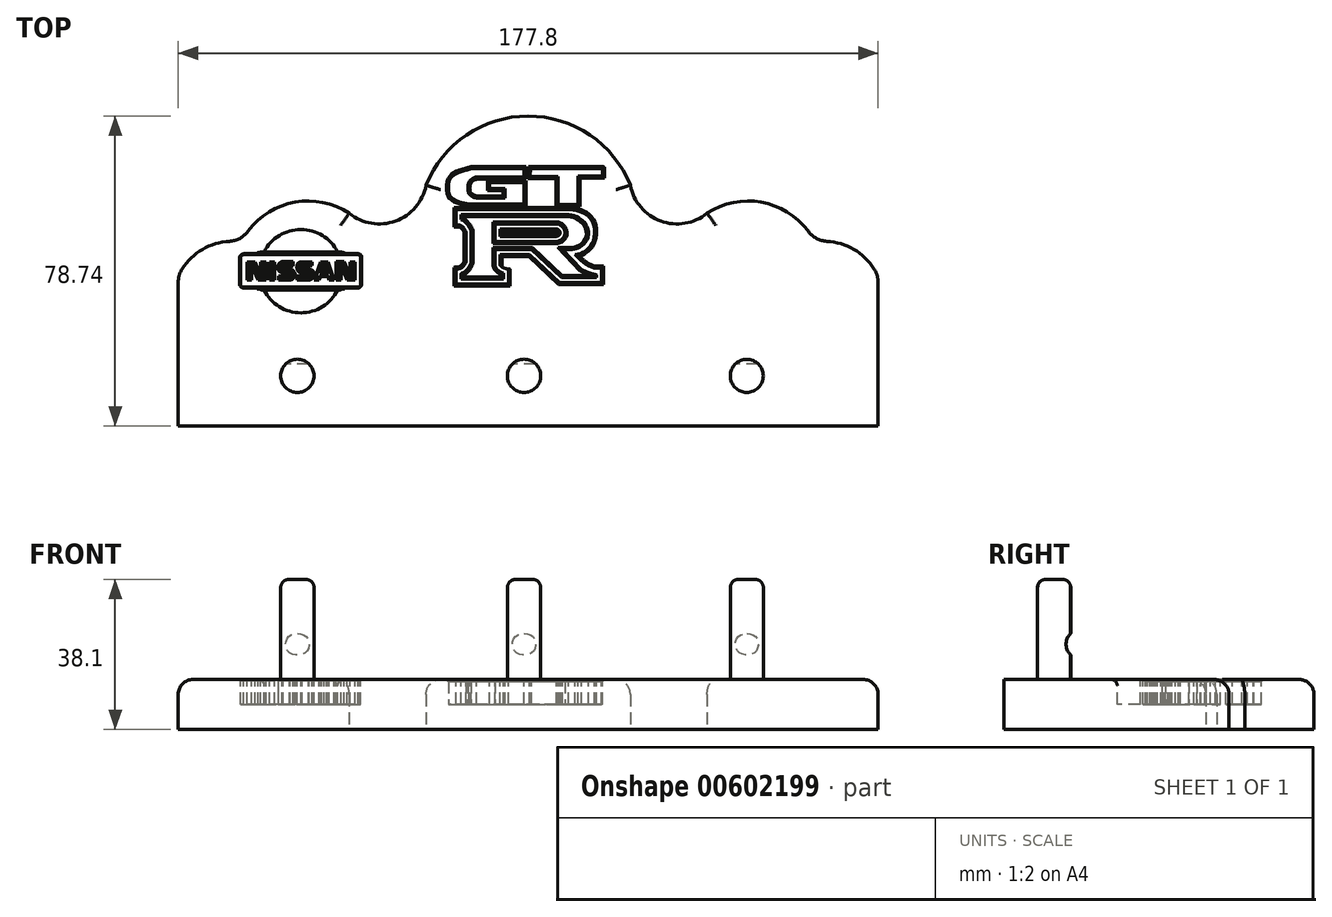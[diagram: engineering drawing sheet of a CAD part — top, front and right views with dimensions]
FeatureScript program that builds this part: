
annotation { "Feature Type Name" : "Feature", "Feature Type Description" : "" }
export const myFeature = defineFeature(function(context is Context, id is Id, definition is map)
    precondition{}
    {
        {
            var Q0;
            Q0=qCreatedBy(makeId("Top.planeOp"),FACE);
            var sketch = newSketch(context, id + "F0", { "sketchPlane" : qUnion([Q0])});
            skLineSegment(sketch, "E0", {"start": v(0, 0) * mm, "end": v(88.9, 0) * mm});
            skLineSegment(sketch, "E1", {"start": v(0, 0) * mm, "end": v(0, 36.5) * mm});
            skArc(sketch, "E2", {"start": v(44.68, 53.17) * mm, "mid": v(30.43, 56.97) * mm, "end": v(17.74, 49.47) * mm});
            skArc(sketch, "E3", {"start": v(88.9, 78.74) * mm, "mid": v(71.93, 73) * mm, "end": v(61.94, 58.13) * mm});
            skLineSegment(sketch, "E4", {"start": v(88.9, 95.72) * mm, "end": v(88.9, -40.01) * mm, "construction": true});
            skPoint(sketch, "E4.endSnap0", {"position": v(88.9, 0) * mm});
            skArc(sketch, "E5", {"start": v(43.45, 54.04) * mm, "mid": v(55.21, 52.07) * mm, "end": v(62.95, 61.15) * mm});
            skArc(sketch, "E6", {"start": v(13, 46.92) * mm, "mid": v(6.17, 44.86) * mm, "end": v(1.02, 39.94) * mm});
            skPoint(sketch, "E7.visualSharp", {"position": v(16.07, 46.79) * mm});
            skArc(sketch, "E7.filletArc", {"start": v(13, 46.92) * mm, "mid": v(15.65, 47.67) * mm, "end": v(17.74, 49.47) * mm});
            skArc(sketch, "E8.MirrorCS", {"start": v(88.9, 78.74) * mm, "mid": v(105.87, 73) * mm, "end": v(115.86, 58.13) * mm});
            skArc(sketch, "E9.MirrorCS", {"start": v(134.35, 54.04) * mm, "mid": v(122.59, 52.07) * mm, "end": v(114.85, 61.15) * mm});
            skArc(sketch, "E10.MirrorCS", {"start": v(133.12, 53.17) * mm, "mid": v(147.37, 56.97) * mm, "end": v(160.06, 49.47) * mm});
            skPoint(sketch, "E11.MirrorP", {"position": v(161.73, 46.79) * mm});
            skArc(sketch, "E12.MirrorCS", {"start": v(164.8, 46.92) * mm, "mid": v(171.63, 44.86) * mm, "end": v(176.78, 39.94) * mm});
            skLineSegment(sketch, "E13.MirrorCS", {"start": v(177.8, 0) * mm, "end": v(177.8, 36.5) * mm});
            skLineSegment(sketch, "E14.MirrorCS", {"start": v(177.8, 0) * mm, "end": v(88.9, 0) * mm});
            skArc(sketch, "E15.MirrorCS", {"start": v(164.8, 46.92) * mm, "mid": v(162.15, 47.67) * mm, "end": v(160.06, 49.47) * mm});
            skPoint(sketch, "E16.visualSharp", {"position": v(0, 38.1) * mm});
            skArc(sketch, "E16.filletArc", {"start": v(1.02, 39.94) * mm, "mid": v(0.26, 38.29) * mm, "end": v(0, 36.5) * mm});
            skPoint(sketch, "E17.visualSharp", {"position": v(177.8, 38.1) * mm});
            skArc(sketch, "E17.filletArc", {"start": v(177.8, 36.5) * mm, "mid": v(177.54, 38.29) * mm, "end": v(176.78, 39.94) * mm});
            skSolve(sketch);
        }
        {
            var Q0;
            Q0=makeQuery(id+"F0.imprint","IMPRINT",FACE,{"disambiguationData":[TD([[makeQuery(id+"F0.imprint","IMPRINT",EDGE,{"derivedFrom":sQuery(id+"F0.wireOp",EDGE,"E0")}),1.0]])]});
            extrude(context, id + "F1", {"entities" : qUnion([Q0]), "depth" : 12.7 * mm, "offsetDistance" : 25.4 * mm});
        }
        {
            var Q0;
            Q0=makeQuery(id+"F1.opExtrude","CAP_FACE",FACE,{"disambiguationData":[OSD([sQuery(id+"F0.wireOp",EDGE,"E0"),sQuery(id+"F0.wireOp",EDGE,"E1"),sQuery(id+"F0.wireOp",EDGE,"E2"),sQuery(id+"F0.wireOp",EDGE,"E3"),sQuery(id+"F0.wireOp",EDGE,"E5"),sQuery(id+"F0.wireOp",EDGE,"E6"),sQuery(id+"F0.wireOp",EDGE,"E7.filletArc"),sQuery(id+"F0.wireOp",EDGE,"E8.MirrorCS"),sQuery(id+"F0.wireOp",EDGE,"E9.MirrorCS"),sQuery(id+"F0.wireOp",EDGE,"E10.MirrorCS"),sQuery(id+"F0.wireOp",EDGE,"E12.MirrorCS"),sQuery(id+"F0.wireOp",EDGE,"E13.MirrorCS"),sQuery(id+"F0.wireOp",EDGE,"E14.MirrorCS"),sQuery(id+"F0.wireOp",EDGE,"E15.MirrorCS"),sQuery(id+"F0.wireOp",EDGE,"E16.filletArc"),sQuery(id+"F0.wireOp",EDGE,"E17.filletArc")])],"isStart":false});
            var sketch = newSketch(context, id + "F2", { "sketchPlane" : qUnion([Q0])});
            skLineSegment(sketch, "E18", {"start": v(89.5, 65.35) * mm, "end": v(107.82, 65.35) * mm});
            skLineSegment(sketch, "E19", {"start": v(107.82, 65.35) * mm, "end": v(107.82, 63.49) * mm});
            skLineSegment(sketch, "E20", {"start": v(107.82, 63.49) * mm, "end": v(101.51, 63.49) * mm});
            skLineSegment(sketch, "E21", {"start": v(101.51, 63.49) * mm, "end": v(101.51, 56.31) * mm});
            skLineSegment(sketch, "E22", {"start": v(101.51, 56.31) * mm, "end": v(96.44, 56.31) * mm});
            skLineSegment(sketch, "E23", {"start": v(96.44, 56.31) * mm, "end": v(96.44, 63.37) * mm});
            skLineSegment(sketch, "E24", {"start": v(96.44, 63.37) * mm, "end": v(89.39, 63.37) * mm});
            skLineSegment(sketch, "E25", {"start": v(89.39, 63.37) * mm, "end": v(89.5, 65.35) * mm});
            skLineSegment(sketch, "E26", {"start": v(75.75, 57.97) * mm, "end": v(83.05, 57.97) * mm});
            skLineSegment(sketch, "E27", {"start": v(83.05, 57.97) * mm, "end": v(83.05, 60.38) * mm});
            skLineSegment(sketch, "E28", {"start": v(83.05, 60.38) * mm, "end": v(79.09, 60.38) * mm});
            skLineSegment(sketch, "E29", {"start": v(79.09, 60.38) * mm, "end": v(79.09, 61.87) * mm});
            skLineSegment(sketch, "E30", {"start": v(79.09, 61.87) * mm, "end": v(87.81, 61.87) * mm});
            skLineSegment(sketch, "E31", {"start": v(87.81, 61.87) * mm, "end": v(87.81, 56.36) * mm});
            skLineSegment(sketch, "E32", {"start": v(87.81, 56.36) * mm, "end": v(73.89, 56.36) * mm});
            skLineSegment(sketch, "E33", {"start": v(75.8, 63.3) * mm, "end": v(87.81, 63.3) * mm});
            skLineSegment(sketch, "E34", {"start": v(87.81, 63.3) * mm, "end": v(87.81, 65.35) * mm});
            skLineSegment(sketch, "E35", {"start": v(87.81, 65.35) * mm, "end": v(74.45, 65.35) * mm});
            skFitSpline(sketch, "E36", {"points": [v(73.89, 56.36) * mm, v(71.04, 57.04) * mm, v(68.94, 58.71) * mm, v(68.75, 61.93) * mm, v(69.25, 63.04) * mm, v(70.8, 64.22) * mm, v(74.45, 65.35) * mm], "startDerivative": vector(-16.25, 2.89) * mm, "endDerivative": vector(19.65, 4.7) * mm});
            skLineSegment(sketch, "E37", {"start": v(70.61, 54.94) * mm, "end": v(99.1, 54.94) * mm});
            skLineSegment(sketch, "E38", {"start": v(73.17, 48.97) * mm, "end": v(73.15, 42.1) * mm});
            skLineSegment(sketch, "E39", {"start": v(70.55, 39.84) * mm, "end": v(70.55, 36) * mm});
            skLineSegment(sketch, "E40", {"start": v(70.55, 36) * mm, "end": v(83.85, 36) * mm});
            skLineSegment(sketch, "E41", {"start": v(83.85, 36) * mm, "end": v(83.85, 39.89) * mm});
            skLineSegment(sketch, "E42", {"start": v(81.75, 41) * mm, "end": v(81.75, 43.5) * mm});
            skLineSegment(sketch, "E43", {"start": v(81.75, 43.5) * mm, "end": v(89.3, 43.5) * mm});
            skLineSegment(sketch, "E44", {"start": v(89.3, 43.5) * mm, "end": v(96.84, 36.45) * mm});
            skLineSegment(sketch, "E45", {"start": v(96.84, 36.45) * mm, "end": v(107.58, 36.45) * mm});
            skLineSegment(sketch, "E46", {"start": v(107.58, 36.45) * mm, "end": v(107.58, 40.07) * mm});
            skFitSpline(sketch, "E47", {"points": [v(70.55, 39.84) * mm, v(71.8, 40.09) * mm, v(72.7, 40.9) * mm, v(73.15, 42.1) * mm], "startDerivative": vector(3.96, 0.32) * mm, "endDerivative": vector(0, 4.08) * mm});
            skLineSegment(sketch, "E48", {"start": v(96.05, 50.06) * mm, "end": v(81.8, 50.06) * mm});
            skLineSegment(sketch, "E49", {"start": v(81.8, 50.06) * mm, "end": v(81.8, 48.18) * mm});
            skLineSegment(sketch, "E50", {"start": v(81.8, 48.18) * mm, "end": v(96.05, 48.18) * mm});
            skFitSpline(sketch, "E51", {"points": [v(96.05, 50.06) * mm, v(96.77, 49.67) * mm, v(96.97, 48.95) * mm, v(96.64, 48.4) * mm, v(96.05, 48.18) * mm], "startDerivative": vector(3.1, 0) * mm, "endDerivative": vector(-2.74, 0) * mm});
            skLineSegment(sketch, "E52.0", {"start": v(71.9, 53.67) * mm, "end": v(71.9, 52.45) * mm});
            skFitSpline(sketch, "E52.1", {"points": [v(70.76, 52.83) * mm, v(70.92, 52.79) * mm, v(71.19, 52.72) * mm, v(71.6, 52.58) * mm, v(71.93, 52.44) * mm, v(72.28, 52.26) * mm, v(72.64, 52.02) * mm, v(72.94, 51.76) * mm, v(73.2, 51.5) * mm, v(73.43, 51.23) * mm, v(73.63, 50.98) * mm, v(73.8, 50.73) * mm, v(73.95, 50.51) * mm, v(74.11, 50.24) * mm, v(74.28, 49.9) * mm, v(74.4, 49.46) * mm, v(74.44, 49.13) * mm, v(74.44, 48.97) * mm]});
            skLineSegment(sketch, "E52.2", {"start": v(74.44, 48.97) * mm, "end": v(74.42, 42.1) * mm});
            skFitSpline(sketch, "E52.3", {"points": [v(70.65, 38.57) * mm, v(70.82, 38.59) * mm, v(71.09, 38.6) * mm, v(71.5, 38.67) * mm, v(71.84, 38.75) * mm, v(72.14, 38.85) * mm, v(72.4, 38.96) * mm, v(72.63, 39.09) * mm, v(72.9, 39.27) * mm, v(73.27, 39.58) * mm, v(73.56, 39.93) * mm, v(73.8, 40.26) * mm, v(73.99, 40.55) * mm, v(74.15, 40.87) * mm, v(74.34, 41.36) * mm, v(74.42, 41.8) * mm, v(74.42, 42.1) * mm]});
            skLineSegment(sketch, "E52.4", {"start": v(71.82, 38.75) * mm, "end": v(71.82, 37.28) * mm});
            skLineSegment(sketch, "E52.5", {"start": v(71.9, 53.67) * mm, "end": v(99.1, 53.67) * mm});
            skLineSegment(sketch, "E52.6", {"start": v(71.82, 37.28) * mm, "end": v(82.58, 37.28) * mm});
            skLineSegment(sketch, "E52.7", {"start": v(106.31, 37.72) * mm, "end": v(106.31, 38.4) * mm});
            skFitSpline(sketch, "E52.8", {"points": [v(102.42, 39.81) * mm, v(102.5, 39.76) * mm, v(102.68, 39.67) * mm, v(103.05, 39.49) * mm, v(103.45, 39.3) * mm, v(103.9, 39.1) * mm, v(104.25, 38.96) * mm, v(104.61, 38.83) * mm, v(105.1, 38.68) * mm, v(105.7, 38.53) * mm, v(106.63, 38.33) * mm, v(107.24, 38.25) * mm, v(107.62, 38.2) * mm]});
            skLineSegment(sketch, "E52.11", {"start": v(97.34, 37.72) * mm, "end": v(106.31, 37.72) * mm});
            skLineSegment(sketch, "E52.12", {"start": v(89.8, 44.78) * mm, "end": v(97.34, 37.72) * mm});
            skLineSegment(sketch, "E52.13", {"start": v(80.48, 44.78) * mm, "end": v(89.8, 44.78) * mm});
            skLineSegment(sketch, "E52.14", {"start": v(80.48, 41.03) * mm, "end": v(80.48, 44.78) * mm});
            skFitSpline(sketch, "E52.15", {"points": [v(80.48, 41.03) * mm, v(80.48, 40.94) * mm, v(80.5, 40.75) * mm, v(80.56, 40.48) * mm, v(80.67, 40.24) * mm, v(80.83, 39.99) * mm, v(80.96, 39.84) * mm, v(81.04, 39.76) * mm, v(81.09, 39.7) * mm, v(81.15, 39.65) * mm, v(81.24, 39.57) * mm, v(81.36, 39.46) * mm, v(81.54, 39.32) * mm, v(81.75, 39.18) * mm, v(81.93, 39.08) * mm, v(82.14, 38.99) * mm, v(82.37, 38.9) * mm, v(82.71, 38.8) * mm, v(82.99, 38.75) * mm, v(83.16, 38.71) * mm, v(83.32, 38.67) * mm, v(83.43, 38.65) * mm, v(83.5, 38.63) * mm]});
            skLineSegment(sketch, "E52.16", {"start": v(82.58, 37.28) * mm, "end": v(82.58, 38.84) * mm});
            skFitSpline(sketch, "E53", {"points": [v(99.1, 53.67) * mm, v(100.84, 53.33) * mm, v(102.68, 52.18) * mm, v(103.86, 50.66) * mm, v(104.2, 49.02) * mm, v(103.86, 47.38) * mm, v(102.96, 46.12) * mm, v(101.7, 45.28) * mm, v(99.8, 44.85) * mm, v(97.67, 44.82) * mm], "startDerivative": vector(15.3, -1.57) * mm, "endDerivative": vector(-17.73, 0.43) * mm});
            skLineSegment(sketch, "E54", {"start": v(97.67, 44.82) * mm, "end": v(102.42, 39.81) * mm});
            skLineSegment(sketch, "E55", {"start": v(70.61, 54.94) * mm, "end": v(70.61, 51.01) * mm});
            skFitSpline(sketch, "E56", {"points": [v(70.61, 51.01) * mm, v(71.55, 51.03) * mm, v(72.28, 50.57) * mm, v(72.9, 49.76) * mm, v(73.17, 48.97) * mm], "startDerivative": vector(3.81, -0.71) * mm, "endDerivative": vector(0.74, -3.33) * mm});
            skLineSegment(sketch, "E57.0", {"start": v(96.05, 51.33) * mm, "end": v(80.53, 51.33) * mm});
            skFitSpline(sketch, "E57.1", {"points": [v(96.05, 51.33) * mm, v(96.23, 51.33) * mm, v(96.58, 51.28) * mm, v(97.03, 51.1) * mm, v(97.4, 50.85) * mm, v(97.7, 50.55) * mm, v(97.95, 50.2) * mm, v(98.13, 49.82) * mm, v(98.24, 49.4) * mm, v(98.27, 48.96) * mm, v(98.2, 48.5) * mm, v(98.02, 48.09) * mm, v(97.8, 47.74) * mm, v(97.51, 47.45) * mm, v(97.19, 47.21) * mm, v(96.71, 46.99) * mm, v(96.32, 46.91) * mm, v(96.05, 46.91) * mm]});
            skLineSegment(sketch, "E57.2", {"start": v(80.53, 46.91) * mm, "end": v(96.05, 46.91) * mm});
            skLineSegment(sketch, "E57.3", {"start": v(80.53, 51.33) * mm, "end": v(80.53, 46.91) * mm});
            skFitSpline(sketch, "E58", {"points": [v(100.8, 43.57) * mm, v(102.39, 43.9) * mm, v(104.04, 44.93) * mm, v(105.07, 46.22) * mm, v(105.7, 48.24) * mm, v(105.66, 50.67) * mm, v(104.85, 52.51) * mm, v(103.57, 53.84) * mm, v(101.98, 54.5) * mm, v(100.33, 54.94) * mm, v(99.1, 54.94) * mm], "startDerivative": vector(16.67, 2.03) * mm, "endDerivative": vector(-14.4, -1.08) * mm});
            skFitSpline(sketch, "E59", {"points": [v(100.8, 43.57) * mm, v(102.06, 42.4) * mm, v(103.3, 41.25) * mm, v(104.9, 40.4) * mm, v(106.07, 40.11) * mm, v(107.58, 40.07) * mm], "startDerivative": vector(6.1, -5.61) * mm, "endDerivative": vector(8.1, 0.07) * mm});
            skFitSpline(sketch, "E60", {"points": [v(75.8, 63.3) * mm, v(74.95, 62.93) * mm, v(73.99, 62.14) * mm, v(73.62, 61.05) * mm, v(73.6, 59.91) * mm, v(73.92, 58.93) * mm, v(74.56, 58.45) * mm, v(75.1, 58.08) * mm, v(75.75, 57.97) * mm], "startDerivative": vector(-6.7, -2.41) * mm, "endDerivative": vector(6.48, -0.32) * mm});
            skFitSpline(sketch, "E61", {"points": [v(81.75, 41) * mm, v(81.84, 40.74) * mm, v(82.47, 40.29) * mm, v(83.3, 39.96) * mm, v(83.85, 39.89) * mm], "startDerivative": vector(0.2, -1.53) * mm, "endDerivative": vector(2.22, -0.16) * mm});
            skSolve(sketch);
        }
        {
            var Q0;
            Q0=makeQuery(id+"F2.imprint","IMPRINT",FACE,{"disambiguationData":[TD([[makeQuery(id+"F2.imprint","IMPRINT",EDGE,{"derivedFrom":sQuery(id+"F2.wireOp",EDGE,"E26")}),-1.0]])]});
            var Q1;
            Q1=makeQuery(id+"F2.imprint","IMPRINT",FACE,{"disambiguationData":[TD([[makeQuery(id+"F2.imprint","IMPRINT",EDGE,{"derivedFrom":sQuery(id+"F2.wireOp",EDGE,"E18")}),-1.0]])]});
            var Q2;
            Q2=makeQuery(id+"F2.imprint","IMPRINT",FACE,{"disambiguationData":[TD([[makeQuery(id+"F2.imprint","IMPRINT",EDGE,{"derivedFrom":sQuery(id+"F2.wireOp",EDGE,"E37")}),-1.0]])]});
            var Q3;
            Q3=makeQuery(id+"F2.imprint","IMPRINT",FACE,{"disambiguationData":[TD([[makeQuery(id+"F2.imprint","IMPRINT",EDGE,{"derivedFrom":sQuery(id+"F2.wireOp",EDGE,"E48")}),-1.0]])]});
            extrude(context, id + "F3", {"entities" : qUnion([Q0, Q1, Q2, Q3]), "operationType" : NewBodyOperationType.REMOVE, "oppositeDirection" : true, "depth" : 6.35 * mm, "offsetDistance" : 25.4 * mm});
        }
        {
            var Q0;
            Q0=makeQuery(id+"F3.boolean.opBoolean","COPY",EDGE,{"derivedFrom":makeQuery(id+"F3.opExtrude","CAP_EDGE",EDGE,{"disambiguationData":[OSD([sQuery(id+"F2.wireOp",EDGE,"E18")])],"isStart":true})});
            var Q1;
            Q1=makeQuery(id+"F3.boolean.opBoolean","COPY",EDGE,{"derivedFrom":makeQuery(id+"F3.opExtrude","CAP_EDGE",EDGE,{"disambiguationData":[OSD([sQuery(id+"F2.wireOp",EDGE,"E25")])],"isStart":true})});
            var Q2;
            Q2=makeQuery(id+"F3.boolean.opBoolean","COPY",EDGE,{"derivedFrom":makeQuery(id+"F3.opExtrude","CAP_EDGE",EDGE,{"disambiguationData":[OSD([sQuery(id+"F2.wireOp",EDGE,"E24")])],"isStart":true})});
            var Q3;
            Q3=makeQuery(id+"F3.boolean.opBoolean","COPY",EDGE,{"derivedFrom":makeQuery(id+"F3.opExtrude","CAP_EDGE",EDGE,{"disambiguationData":[OSD([sQuery(id+"F2.wireOp",EDGE,"E23")])],"isStart":true})});
            var Q4;
            Q4=makeQuery(id+"F3.boolean.opBoolean","COPY",EDGE,{"derivedFrom":makeQuery(id+"F3.opExtrude","CAP_EDGE",EDGE,{"disambiguationData":[OSD([sQuery(id+"F2.wireOp",EDGE,"E22")])],"isStart":true})});
            var Q5;
            Q5=makeQuery(id+"F3.boolean.opBoolean","COPY",EDGE,{"derivedFrom":makeQuery(id+"F3.opExtrude","CAP_EDGE",EDGE,{"disambiguationData":[OSD([sQuery(id+"F2.wireOp",EDGE,"E21")])],"isStart":true})});
            var Q6;
            Q6=makeQuery(id+"F3.boolean.opBoolean","COPY",EDGE,{"derivedFrom":makeQuery(id+"F3.opExtrude","CAP_EDGE",EDGE,{"disambiguationData":[OSD([sQuery(id+"F2.wireOp",EDGE,"E20")])],"isStart":true})});
            var Q7;
            Q7=makeQuery(id+"F3.boolean.opBoolean","COPY",EDGE,{"derivedFrom":makeQuery(id+"F3.opExtrude","CAP_EDGE",EDGE,{"disambiguationData":[OSD([sQuery(id+"F2.wireOp",EDGE,"E19")])],"isStart":true})});
            var Q8;
            Q8=makeQuery(id+"F3.boolean.opBoolean","COPY",EDGE,{"derivedFrom":makeQuery(id+"F3.opExtrude","CAP_EDGE",EDGE,{"disambiguationData":[OSD([sQuery(id+"F2.wireOp",EDGE,"E33")])],"isStart":true})});
            var Q9;
            Q9=makeQuery(id+"F3.boolean.opBoolean","COPY",EDGE,{"derivedFrom":makeQuery(id+"F3.opExtrude","CAP_EDGE",EDGE,{"disambiguationData":[OSD([sQuery(id+"F2.wireOp",EDGE,"E35")])],"isStart":true})});
            var Q10;
            Q10=makeQuery(id+"F3.boolean.opBoolean","COPY",EDGE,{"derivedFrom":makeQuery(id+"F3.opExtrude","CAP_EDGE",EDGE,{"disambiguationData":[OSD([sQuery(id+"F2.wireOp",EDGE,"E34")])],"isStart":true})});
            var Q11;
            Q11=makeQuery(id+"F3.boolean.opBoolean","COPY",EDGE,{"derivedFrom":makeQuery(id+"F3.opExtrude","CAP_EDGE",EDGE,{"disambiguationData":[OSD([sQuery(id+"F2.wireOp",EDGE,"E36")])],"isStart":true})});
            var Q12;
            Q12=makeQuery(id+"F3.boolean.opBoolean","COPY",EDGE,{"derivedFrom":makeQuery(id+"F3.opExtrude","CAP_EDGE",EDGE,{"disambiguationData":[OSD([sQuery(id+"F2.wireOp",EDGE,"E60")])],"isStart":true})});
            var Q13;
            Q13=makeQuery(id+"F3.boolean.opBoolean","COPY",EDGE,{"derivedFrom":makeQuery(id+"F3.opExtrude","CAP_EDGE",EDGE,{"disambiguationData":[OSD([sQuery(id+"F2.wireOp",EDGE,"E29")])],"isStart":true})});
            var Q14;
            Q14=makeQuery(id+"F3.boolean.opBoolean","COPY",EDGE,{"derivedFrom":makeQuery(id+"F3.opExtrude","CAP_EDGE",EDGE,{"disambiguationData":[OSD([sQuery(id+"F2.wireOp",EDGE,"E30")])],"isStart":true})});
            var Q15;
            Q15=makeQuery(id+"F3.boolean.opBoolean","COPY",EDGE,{"derivedFrom":makeQuery(id+"F3.opExtrude","CAP_EDGE",EDGE,{"disambiguationData":[OSD([sQuery(id+"F2.wireOp",EDGE,"E28")])],"isStart":true})});
            var Q16;
            Q16=makeQuery(id+"F3.boolean.opBoolean","COPY",EDGE,{"derivedFrom":makeQuery(id+"F3.opExtrude","CAP_EDGE",EDGE,{"disambiguationData":[OSD([sQuery(id+"F2.wireOp",EDGE,"E27")])],"isStart":true})});
            var Q17;
            Q17=makeQuery(id+"F3.boolean.opBoolean","COPY",EDGE,{"derivedFrom":makeQuery(id+"F3.opExtrude","CAP_EDGE",EDGE,{"disambiguationData":[OSD([sQuery(id+"F2.wireOp",EDGE,"E31")])],"isStart":true})});
            var Q18;
            Q18=makeQuery(id+"F3.boolean.opBoolean","COPY",EDGE,{"derivedFrom":makeQuery(id+"F3.opExtrude","CAP_EDGE",EDGE,{"disambiguationData":[OSD([sQuery(id+"F2.wireOp",EDGE,"E32")])],"isStart":true})});
            var Q19;
            Q19=makeQuery(id+"F3.boolean.opBoolean","COPY",EDGE,{"derivedFrom":makeQuery(id+"F3.opExtrude","CAP_EDGE",EDGE,{"disambiguationData":[OSD([sQuery(id+"F2.wireOp",EDGE,"E52.5")])],"isStart":true})});
            var Q20;
            Q20=makeQuery(id+"F3.boolean.opBoolean","SPLIT",FACE,{"disambiguationData":[TD([makeQuery(id+"F3.opExtrude","SWEPT_FACE",FACE,{"disambiguationData":[OSD([sQuery(id+"F2.wireOp",EDGE,"E52.0")])]})])],"derivedFrom":makeQuery(id+"F1.opExtrude","CAP_FACE",FACE,{"disambiguationData":[OSD([sQuery(id+"F0.wireOp",EDGE,"E0"),sQuery(id+"F0.wireOp",EDGE,"E1"),sQuery(id+"F0.wireOp",EDGE,"E2"),sQuery(id+"F0.wireOp",EDGE,"E3"),sQuery(id+"F0.wireOp",EDGE,"E5"),sQuery(id+"F0.wireOp",EDGE,"E6"),sQuery(id+"F0.wireOp",EDGE,"E7.filletArc"),sQuery(id+"F0.wireOp",EDGE,"E8.MirrorCS"),sQuery(id+"F0.wireOp",EDGE,"E9.MirrorCS"),sQuery(id+"F0.wireOp",EDGE,"E10.MirrorCS"),sQuery(id+"F0.wireOp",EDGE,"E12.MirrorCS"),sQuery(id+"F0.wireOp",EDGE,"E13.MirrorCS"),sQuery(id+"F0.wireOp",EDGE,"E14.MirrorCS"),sQuery(id+"F0.wireOp",EDGE,"E15.MirrorCS"),sQuery(id+"F0.wireOp",EDGE,"E16.filletArc"),sQuery(id+"F0.wireOp",EDGE,"E17.filletArc")])],"isStart":false})});
            var Q21;
            Q21=makeQuery(id+"F3.boolean.opBoolean","SPLIT",FACE,{"disambiguationData":[TD([makeQuery(id+"F3.opExtrude","SWEPT_FACE",FACE,{"disambiguationData":[OSD([sQuery(id+"F2.wireOp",EDGE,"E48")])]})])],"derivedFrom":makeQuery(id+"F1.opExtrude","CAP_FACE",FACE,{"disambiguationData":[OSD([sQuery(id+"F0.wireOp",EDGE,"E0"),sQuery(id+"F0.wireOp",EDGE,"E1"),sQuery(id+"F0.wireOp",EDGE,"E2"),sQuery(id+"F0.wireOp",EDGE,"E3"),sQuery(id+"F0.wireOp",EDGE,"E5"),sQuery(id+"F0.wireOp",EDGE,"E6"),sQuery(id+"F0.wireOp",EDGE,"E7.filletArc"),sQuery(id+"F0.wireOp",EDGE,"E8.MirrorCS"),sQuery(id+"F0.wireOp",EDGE,"E9.MirrorCS"),sQuery(id+"F0.wireOp",EDGE,"E10.MirrorCS"),sQuery(id+"F0.wireOp",EDGE,"E12.MirrorCS"),sQuery(id+"F0.wireOp",EDGE,"E13.MirrorCS"),sQuery(id+"F0.wireOp",EDGE,"E14.MirrorCS"),sQuery(id+"F0.wireOp",EDGE,"E15.MirrorCS"),sQuery(id+"F0.wireOp",EDGE,"E16.filletArc"),sQuery(id+"F0.wireOp",EDGE,"E17.filletArc")])],"isStart":false})});
            var Q22;
            Q22=makeQuery(id+"F3.boolean.opBoolean","COPY",EDGE,{"derivedFrom":makeQuery(id+"F3.opExtrude","CAP_EDGE",EDGE,{"disambiguationData":[OSD([sQuery(id+"F2.wireOp",EDGE,"E37")])],"isStart":true})});
            var Q23;
            Q23=makeQuery(id+"F3.boolean.opBoolean","COPY",EDGE,{"derivedFrom":makeQuery(id+"F3.opExtrude","CAP_EDGE",EDGE,{"disambiguationData":[OSD([sQuery(id+"F2.wireOp",EDGE,"E58")])],"isStart":true})});
            var Q24;
            Q24=makeQuery(id+"F3.boolean.opBoolean","COPY",EDGE,{"derivedFrom":makeQuery(id+"F3.opExtrude","CAP_EDGE",EDGE,{"disambiguationData":[OSD([sQuery(id+"F2.wireOp",EDGE,"E41")])],"isStart":true})});
            var Q25;
            Q25=makeQuery(id+"F3.boolean.opBoolean","COPY",EDGE,{"derivedFrom":makeQuery(id+"F3.opExtrude","CAP_EDGE",EDGE,{"disambiguationData":[OSD([sQuery(id+"F2.wireOp",EDGE,"E44")])],"isStart":true})});
            var Q26;
            Q26=makeQuery(id+"F3.boolean.opBoolean","COPY",EDGE,{"derivedFrom":makeQuery(id+"F3.opExtrude","CAP_EDGE",EDGE,{"disambiguationData":[OSD([sQuery(id+"F2.wireOp",EDGE,"E43")])],"isStart":true})});
            var Q27;
            Q27=makeQuery(id+"F3.boolean.opBoolean","COPY",EDGE,{"derivedFrom":makeQuery(id+"F3.opExtrude","CAP_EDGE",EDGE,{"disambiguationData":[OSD([sQuery(id+"F2.wireOp",EDGE,"E59")])],"isStart":true})});
            var Q28;
            Q28=makeQuery(id+"F3.boolean.opBoolean","COPY",EDGE,{"derivedFrom":makeQuery(id+"F3.opExtrude","CAP_EDGE",EDGE,{"disambiguationData":[OSD([sQuery(id+"F2.wireOp",EDGE,"E46")])],"isStart":true})});
            var Q29;
            Q29=makeQuery(id+"F3.boolean.opBoolean","COPY",EDGE,{"derivedFrom":makeQuery(id+"F3.opExtrude","CAP_EDGE",EDGE,{"disambiguationData":[OSD([sQuery(id+"F2.wireOp",EDGE,"E45")])],"isStart":true})});
            var Q30;
            Q30=makeQuery(id+"F3.boolean.opBoolean","COPY",EDGE,{"derivedFrom":makeQuery(id+"F3.opExtrude","CAP_EDGE",EDGE,{"disambiguationData":[OSD([sQuery(id+"F2.wireOp",EDGE,"E40")])],"isStart":true})});
            var Q31;
            Q31=makeQuery(id+"F3.boolean.opBoolean","COPY",EDGE,{"derivedFrom":makeQuery(id+"F3.opExtrude","CAP_EDGE",EDGE,{"disambiguationData":[OSD([sQuery(id+"F2.wireOp",EDGE,"E39")])],"isStart":true})});
            var Q32;
            Q32=makeQuery(id+"F3.boolean.opBoolean","COPY",EDGE,{"derivedFrom":makeQuery(id+"F3.opExtrude","CAP_EDGE",EDGE,{"disambiguationData":[OSD([sQuery(id+"F2.wireOp",EDGE,"E47")])],"isStart":true})});
            var Q33;
            Q33=makeQuery(id+"F3.boolean.opBoolean","COPY",EDGE,{"derivedFrom":makeQuery(id+"F3.opExtrude","CAP_EDGE",EDGE,{"disambiguationData":[OSD([sQuery(id+"F2.wireOp",EDGE,"E38")])],"isStart":true})});
            var Q34;
            Q34=makeQuery(id+"F3.boolean.opBoolean","COPY",EDGE,{"derivedFrom":makeQuery(id+"F3.opExtrude","CAP_EDGE",EDGE,{"disambiguationData":[OSD([sQuery(id+"F2.wireOp",EDGE,"E56")])],"isStart":true})});
            var Q35;
            Q35=makeQuery(id+"F3.boolean.opBoolean","COPY",EDGE,{"derivedFrom":makeQuery(id+"F3.opExtrude","CAP_EDGE",EDGE,{"disambiguationData":[OSD([sQuery(id+"F2.wireOp",EDGE,"E55")])],"isStart":true})});
            chamfer(context, id + "F4", {"entities" : qUnion([Q0, Q1, Q2, Q3, Q4, Q5, Q6, Q7, Q8, Q9, Q10, Q11, Q12, Q13, Q14, Q15, Q16, Q17, Q18, Q19, Q20, Q21, Q22, Q23, Q24, Q25, Q26, Q27, Q28, Q29, Q30, Q31, Q32, Q33, Q34, Q35]), "width" : 0.5 * mm, "tangentPropagation" : true});
        }
        {
            var Q0;
            {var subQ0=sQuery(id+"F0.wireOp",EDGE,"E12.MirrorCS");var subQ1=sQuery(id+"F0.wireOp",EDGE,"E10.MirrorCS");var subQ2=sQuery(id+"F0.wireOp",EDGE,"E9.MirrorCS");var subQ3=sQuery(id+"F0.wireOp",EDGE,"E7.filletArc");var subQ4=sQuery(id+"F0.wireOp",EDGE,"E6");var subQ5=sQuery(id+"F0.wireOp",EDGE,"E5");var subQ6=sQuery(id+"F0.wireOp",EDGE,"E14.MirrorCS");var subQ7=sQuery(id+"F0.wireOp",EDGE,"E0");var subQ8=sQuery(id+"F0.wireOp",EDGE,"E1");var subQ9=sQuery(id+"F0.wireOp",EDGE,"E2");var subQ10=sQuery(id+"F0.wireOp",EDGE,"E8.MirrorCS");var subQ11=sQuery(id+"F0.wireOp",EDGE,"E3");var subQ12=sQuery(id+"F0.wireOp",EDGE,"E13.MirrorCS");var subQ13=sQuery(id+"F0.wireOp",EDGE,"E15.MirrorCS");var subQ14=sQuery(id+"F0.wireOp",EDGE,"E16.filletArc");var subQ15=sQuery(id+"F0.wireOp",EDGE,"E17.filletArc");Q0=makeQuery(id+"F3.boolean.opBoolean","SPLIT",FACE,{"disambiguationData":[TD([makeQuery(id+"F1.opExtrude","SWEPT_FACE",FACE,{"disambiguationData":[OSD([subQ8])]})])],"derivedFrom":makeQuery(id+"F1.opExtrude","CAP_FACE",FACE,{"disambiguationData":[OSD([subQ7,subQ8,subQ9,subQ11,subQ5,subQ4,subQ3,subQ10,subQ2,subQ1,subQ0,subQ12,subQ6,subQ13,subQ14,subQ15])],"isStart":false})});}
            var sketch = newSketch(context, id + "F5", { "sketchPlane" : qUnion([Q0])});
            skArc(sketch, "E62", {"start": v(40.5, 44.26) * mm, "mid": v(31.16, 49.94) * mm, "end": v(21.8, 44.26) * mm});
            skLineSegment(sketch, "E63", {"start": v(21.8, 44.26) * mm, "end": v(40.5, 44.26) * mm});
            skLineSegment(sketch, "E64", {"start": v(21.86, 34.6) * mm, "end": v(40.47, 34.6) * mm});
            skArc(sketch, "E65", {"start": v(21.86, 34.6) * mm, "mid": v(31.16, 28.74) * mm, "end": v(40.47, 34.6) * mm});
            skLineSegment(sketch, "E66", {"start": v(17.43, 37.11) * mm, "end": v(17.43, 41.71) * mm});
            skLineSegment(sketch, "E67", {"start": v(17.43, 41.71) * mm, "end": v(19.53, 41.71) * mm});
            skLineSegment(sketch, "E68", {"start": v(19.53, 41.71) * mm, "end": v(20.96, 38.22) * mm});
            skLineSegment(sketch, "E69", {"start": v(20.96, 38.22) * mm, "end": v(20.96, 41.68) * mm});
            skLineSegment(sketch, "E70", {"start": v(20.96, 41.68) * mm, "end": v(22.3, 41.68) * mm});
            skLineSegment(sketch, "E71", {"start": v(22.3, 41.68) * mm, "end": v(22.3, 37.05) * mm});
            skLineSegment(sketch, "E72", {"start": v(22.3, 37.05) * mm, "end": v(20.23, 37.05) * mm});
            skLineSegment(sketch, "E73", {"start": v(20.23, 37.05) * mm, "end": v(18.7, 40.71) * mm});
            skLineSegment(sketch, "E74", {"start": v(18.7, 40.71) * mm, "end": v(18.7, 37.11) * mm});
            skLineSegment(sketch, "E75", {"start": v(18.7, 37.11) * mm, "end": v(17.43, 37.11) * mm});
            skLineSegment(sketch, "E76", {"start": v(23.21, 41.7) * mm, "end": v(24.52, 41.7) * mm});
            skLineSegment(sketch, "E77", {"start": v(24.52, 41.7) * mm, "end": v(24.52, 37.06) * mm});
            skLineSegment(sketch, "E78", {"start": v(24.52, 37.06) * mm, "end": v(23.23, 37.06) * mm});
            skLineSegment(sketch, "E79", {"start": v(23.23, 37.06) * mm, "end": v(23.21, 41.7) * mm});
            skLineSegment(sketch, "E80", {"start": v(34.46, 37.06) * mm, "end": v(36.12, 41.7) * mm});
            skLineSegment(sketch, "E81", {"start": v(36.12, 41.7) * mm, "end": v(38.01, 41.7) * mm});
            skLineSegment(sketch, "E82", {"start": v(38.01, 41.7) * mm, "end": v(39.65, 37.08) * mm});
            skLineSegment(sketch, "E83", {"start": v(39.65, 37.08) * mm, "end": v(38.36, 37.08) * mm});
            skLineSegment(sketch, "E84", {"start": v(38.36, 37.08) * mm, "end": v(38.05, 37.9) * mm});
            skLineSegment(sketch, "E85", {"start": v(38.05, 37.9) * mm, "end": v(36.1, 37.9) * mm});
            skLineSegment(sketch, "E86", {"start": v(36.1, 37.9) * mm, "end": v(35.76, 37.04) * mm});
            skLineSegment(sketch, "E87", {"start": v(35.76, 37.04) * mm, "end": v(34.46, 37.06) * mm});
            skLineSegment(sketch, "E88", {"start": v(36.42, 38.94) * mm, "end": v(37.04, 40.68) * mm});
            skLineSegment(sketch, "E89", {"start": v(37.04, 40.68) * mm, "end": v(37.72, 38.92) * mm});
            skLineSegment(sketch, "E90", {"start": v(37.72, 38.92) * mm, "end": v(36.42, 38.94) * mm});
            skLineSegment(sketch, "E91", {"start": v(40.07, 37.09) * mm, "end": v(40.07, 41.72) * mm});
            skLineSegment(sketch, "E92", {"start": v(40.07, 41.72) * mm, "end": v(42.18, 41.72) * mm});
            skLineSegment(sketch, "E93", {"start": v(42.18, 41.72) * mm, "end": v(43.63, 38.18) * mm});
            skLineSegment(sketch, "E94", {"start": v(43.63, 38.18) * mm, "end": v(43.63, 41.69) * mm});
            skLineSegment(sketch, "E95", {"start": v(43.63, 41.69) * mm, "end": v(44.91, 41.69) * mm});
            skLineSegment(sketch, "E96", {"start": v(44.91, 41.69) * mm, "end": v(44.91, 37.06) * mm});
            skLineSegment(sketch, "E97", {"start": v(44.91, 37.06) * mm, "end": v(42.88, 37.06) * mm});
            skLineSegment(sketch, "E98", {"start": v(42.88, 37.06) * mm, "end": v(41.38, 40.73) * mm});
            skLineSegment(sketch, "E99", {"start": v(41.38, 40.73) * mm, "end": v(41.38, 37.07) * mm});
            skLineSegment(sketch, "E100", {"start": v(41.38, 37.07) * mm, "end": v(40.07, 37.09) * mm});
            skLineSegment(sketch, "E101", {"start": v(28.4, 39.86) * mm, "end": v(26.59, 39.86) * mm});
            skLineSegment(sketch, "E102", {"start": v(26.59, 39.86) * mm, "end": v(26.59, 40.68) * mm});
            skLineSegment(sketch, "E103", {"start": v(26.59, 40.68) * mm, "end": v(29.22, 40.68) * mm});
            skLineSegment(sketch, "E104", {"start": v(29.22, 40.68) * mm, "end": v(29.22, 41.72) * mm});
            skLineSegment(sketch, "E105", {"start": v(29.22, 41.72) * mm, "end": v(26.34, 41.72) * mm});
            skLineSegment(sketch, "E106", {"start": v(26.64, 38.92) * mm, "end": v(28.26, 38.92) * mm});
            skLineSegment(sketch, "E107", {"start": v(28.26, 38.92) * mm, "end": v(28.26, 38.13) * mm});
            skLineSegment(sketch, "E108", {"start": v(28.26, 38.13) * mm, "end": v(25.45, 38.13) * mm});
            skLineSegment(sketch, "E109", {"start": v(25.45, 38.13) * mm, "end": v(25.45, 37.08) * mm});
            skLineSegment(sketch, "E110", {"start": v(25.45, 37.08) * mm, "end": v(28.48, 37.08) * mm});
            skFitSpline(sketch, "E111", {"points": [v(26.34, 41.72) * mm, v(25.76, 41.42) * mm, v(25.4, 40.9) * mm, v(25.33, 40.32) * mm, v(25.46, 39.55) * mm, v(25.76, 39.22) * mm, v(26.34, 38.98) * mm, v(26.64, 38.92) * mm], "startDerivative": vector(-4.03, -1.59) * mm, "endDerivative": vector(2.58, -0.3) * mm});
            skPoint(sketch, "E112.3.internal.snap0", {"position": v(28.26, 38.52) * mm});
            skFitSpline(sketch, "E112", {"points": [v(28.4, 39.86) * mm, v(29.03, 39.64) * mm, v(29.47, 39.17) * mm, v(29.66, 38.52) * mm, v(29.47, 37.77) * mm, v(28.92, 37.22) * mm, v(28.48, 37.08) * mm], "startDerivative": vector(3.99, -0.96) * mm, "endDerivative": vector(-3.1, -0.58) * mm});
            skLineSegment(sketch, "E113", {"start": v(31.4, 38.91) * mm, "end": v(33.15, 38.91) * mm});
            skLineSegment(sketch, "E114", {"start": v(33.15, 38.91) * mm, "end": v(33.15, 38.1) * mm});
            skLineSegment(sketch, "E115", {"start": v(33.15, 38.1) * mm, "end": v(30.25, 38.1) * mm});
            skLineSegment(sketch, "E116", {"start": v(30.25, 38.1) * mm, "end": v(30.25, 37.05) * mm});
            skLineSegment(sketch, "E117", {"start": v(30.25, 37.05) * mm, "end": v(33.29, 37.05) * mm});
            skLineSegment(sketch, "E118", {"start": v(31.2, 41.71) * mm, "end": v(34.04, 41.71) * mm});
            skLineSegment(sketch, "E119", {"start": v(34.04, 41.71) * mm, "end": v(34.04, 40.71) * mm});
            skLineSegment(sketch, "E120", {"start": v(34.04, 40.71) * mm, "end": v(31.43, 40.71) * mm});
            skLineSegment(sketch, "E121", {"start": v(31.43, 40.71) * mm, "end": v(31.43, 39.9) * mm});
            skLineSegment(sketch, "E122", {"start": v(31.43, 39.9) * mm, "end": v(33.12, 39.9) * mm});
            skFitSpline(sketch, "E123", {"points": [v(31.4, 38.91) * mm, v(30.86, 39.06) * mm, v(30.4, 39.43) * mm, v(30.17, 39.91) * mm, v(30.14, 40.64) * mm, v(30.38, 41.2) * mm, v(30.73, 41.53) * mm, v(31.2, 41.71) * mm], "startDerivative": vector(-3.88, 0.72) * mm, "endDerivative": vector(3.64, 1.1) * mm});
            skFitSpline(sketch, "E124", {"points": [v(33.12, 39.9) * mm, v(33.64, 39.77) * mm, v(34.13, 39.48) * mm, v(34.44, 38.91) * mm, v(34.48, 38.39) * mm, v(34.37, 37.96) * mm, v(34.14, 37.57) * mm, v(33.77, 37.23) * mm, v(33.29, 37.05) * mm], "startDerivative": vector(4.16, -0.8) * mm, "endDerivative": vector(-4.06, -1.22) * mm});
            skLineSegment(sketch, "E125.bottom", {"start": v(16.6, 43.5) * mm, "end": v(45.83, 43.5) * mm});
            skLineSegment(sketch, "E125.top", {"start": v(16.57, 35.3) * mm, "end": v(45.7, 35.3) * mm});
            skLineSegment(sketch, "E125.left", {"start": v(15.82, 42.7) * mm, "end": v(15.82, 36.13) * mm});
            skLineSegment(sketch, "E125.right", {"start": v(46.35, 42.9) * mm, "end": v(46.35, 35.94) * mm});
            skArc(sketch, "E126", {"start": v(46.35, 42.9) * mm, "mid": v(46.2, 43.3) * mm, "end": v(45.83, 43.5) * mm});
            skArc(sketch, "E127", {"start": v(16.6, 43.5) * mm, "mid": v(16.06, 43.25) * mm, "end": v(15.82, 42.7) * mm});
            skArc(sketch, "E128", {"start": v(15.82, 36.13) * mm, "mid": v(16.03, 35.57) * mm, "end": v(16.57, 35.3) * mm});
            skArc(sketch, "E129", {"start": v(45.7, 35.3) * mm, "mid": v(46.13, 35.5) * mm, "end": v(46.35, 35.94) * mm});
            skSolve(sketch);
        }
        {
            var Q0;
            Q0 = qSketchRegion(id + "F5", true);
            var Q1;
            Q1=makeQuery(id+"F5.imprint","IMPRINT",FACE,{"disambiguationData":[TD([[makeQuery(id+"F5.imprint","IMPRINT",EDGE,{"derivedFrom":sQuery(id+"F5.wireOp",EDGE,"E88")}),-1.0]])]});
            extrude(context, id + "F6", {"entities" : qUnion([Q0, Q1]), "operationType" : NewBodyOperationType.REMOVE, "oppositeDirection" : true, "depth" : 6.35 * mm, "offsetDistance" : 25.4 * mm});
        }
        {
            var Q0;
            {var subQ21=sQuery(id+"F0.wireOp",EDGE,"E12.MirrorCS");var subQ23=sQuery(id+"F0.wireOp",EDGE,"E10.MirrorCS");var subQ25=sQuery(id+"F0.wireOp",EDGE,"E9.MirrorCS");var subQ27=sQuery(id+"F0.wireOp",EDGE,"E7.filletArc");var subQ29=sQuery(id+"F0.wireOp",EDGE,"E6");var subQ33=sQuery(id+"F0.wireOp",EDGE,"E5");var subQ37=sQuery(id+"F0.wireOp",EDGE,"E14.MirrorCS");var subQ38=sQuery(id+"F0.wireOp",EDGE,"E0");var subQ42=sQuery(id+"F0.wireOp",EDGE,"E1");var subQ43=makeQuery(id+"F1.opExtrude","SWEPT_FACE",FACE,{"disambiguationData":[OSD([subQ42])]});var subQ46=sQuery(id+"F0.wireOp",EDGE,"E2");var subQ49=sQuery(id+"F0.wireOp",EDGE,"E8.MirrorCS");var subQ50=sQuery(id+"F0.wireOp",EDGE,"E3");var subQ54=sQuery(id+"F0.wireOp",EDGE,"E13.MirrorCS");var subQ56=sQuery(id+"F0.wireOp",EDGE,"E15.MirrorCS");var subQ58=sQuery(id+"F0.wireOp",EDGE,"E16.filletArc");var subQ61=sQuery(id+"F0.wireOp",EDGE,"E17.filletArc");Q0=makeQuery(id+"F6.boolean.opBoolean","SPLIT",FACE,{"disambiguationData":[TD([subQ43])],"derivedFrom":makeQuery(id+"F3.boolean.opBoolean","SPLIT",FACE,{"disambiguationData":[TD([subQ43])],"derivedFrom":makeQuery(id+"F1.opExtrude","CAP_FACE",FACE,{"disambiguationData":[OSD([subQ38,subQ42,subQ46,subQ50,subQ33,subQ29,subQ27,subQ49,subQ25,subQ23,subQ21,subQ54,subQ37,subQ56,subQ58,subQ61])],"isStart":false})})});}
            var sketch = newSketch(context, id + "F7", { "sketchPlane" : qUnion([Q0])});
            skSolve(sketch);
        }
        {
            var Q0;
            Q0=makeQuery(id+"F1.opExtrude","CAP_EDGE",EDGE,{"disambiguationData":[OSD([sQuery(id+"F0.wireOp",EDGE,"E5")])],"isStart":false});
            var Q1;
            Q1=makeQuery(id+"F1.opExtrude","CAP_EDGE",EDGE,{"disambiguationData":[OSD([sQuery(id+"F0.wireOp",EDGE,"E2")])],"isStart":false});
            var Q2;
            Q2=makeQuery(id+"F1.opExtrude","CAP_EDGE",EDGE,{"disambiguationData":[OSD([sQuery(id+"F0.wireOp",EDGE,"E3"),sQuery(id+"F0.wireOp",EDGE,"E8.MirrorCS")])],"isStart":false});
            var Q3;
            Q3=makeQuery(id+"F1.opExtrude","CAP_EDGE",EDGE,{"disambiguationData":[OSD([sQuery(id+"F0.wireOp",EDGE,"E10.MirrorCS")])],"isStart":false});
            var Q4;
            Q4=makeQuery(id+"F1.opExtrude","CAP_EDGE",EDGE,{"disambiguationData":[OSD([sQuery(id+"F0.wireOp",EDGE,"E9.MirrorCS")])],"isStart":false});
            var Q5;
            Q5=makeQuery(id+"F1.opExtrude","CAP_EDGE",EDGE,{"disambiguationData":[OSD([sQuery(id+"F0.wireOp",EDGE,"E12.MirrorCS")])],"isStart":false});
            var Q6;
            Q6=makeQuery(id+"F1.opExtrude","CAP_EDGE",EDGE,{"disambiguationData":[OSD([sQuery(id+"F0.wireOp",EDGE,"E15.MirrorCS")])],"isStart":false});
            fillet(context, id + "F8", {"entities" : qUnion([Q0, Q1, Q2, Q3, Q4, Q5, Q6]), "radius" : 3.8 * mm, "tangentPropagation" : true, "allowEdgeOverflow" : false});
        }
        {
            var Q0;
            Q0=makeQuery(id+"F3.boolean.opBoolean","COPY",EDGE,{"derivedFrom":makeQuery(id+"F3.opExtrude","CAP_EDGE",EDGE,{"disambiguationData":[OSD([sQuery(id+"F2.wireOp",EDGE,"E42")])],"isStart":true})});
            chamfer(context, id + "F9", {"entities" : qUnion([Q0]), "width" : 0.5 * mm, "tangentPropagation" : true});
        }
        {
            var Q0;
            {var subQ27=sQuery(id+"F0.wireOp",EDGE,"E12.MirrorCS");var subQ32=sQuery(id+"F0.wireOp",EDGE,"E10.MirrorCS");var subQ36=sQuery(id+"F0.wireOp",EDGE,"E9.MirrorCS");var subQ43=sQuery(id+"F0.wireOp",EDGE,"E7.filletArc");var subQ50=sQuery(id+"F0.wireOp",EDGE,"E6");var subQ54=sQuery(id+"F0.wireOp",EDGE,"E5");var subQ58=sQuery(id+"F0.wireOp",EDGE,"E14.MirrorCS");var subQ59=sQuery(id+"F0.wireOp",EDGE,"E0");var subQ65=sQuery(id+"F0.wireOp",EDGE,"E1");var subQ66=makeQuery(id+"F1.opExtrude","SWEPT_FACE",FACE,{"disambiguationData":[OSD([subQ65])]});var subQ71=sQuery(id+"F0.wireOp",EDGE,"E2");var subQ79=sQuery(id+"F0.wireOp",EDGE,"E8.MirrorCS");var subQ80=sQuery(id+"F0.wireOp",EDGE,"E3");var subQ82=sQuery(id+"F0.wireOp",EDGE,"E13.MirrorCS");var subQ84=sQuery(id+"F0.wireOp",EDGE,"E15.MirrorCS");var subQ86=sQuery(id+"F0.wireOp",EDGE,"E16.filletArc");var subQ88=sQuery(id+"F0.wireOp",EDGE,"E17.filletArc");Q0=makeQuery(id+"FvO2wPh7fnTy2tx_1.boolean.opBoolean","SPLIT",FACE,{"disambiguationData":[TD([subQ66])],"derivedFrom":makeQuery(id+"F6.boolean.opBoolean","SPLIT",FACE,{"disambiguationData":[TD([subQ66])],"derivedFrom":makeQuery(id+"F3.boolean.opBoolean","SPLIT",FACE,{"disambiguationData":[TD([subQ66])],"derivedFrom":makeQuery(id+"F1.opExtrude","CAP_FACE",FACE,{"disambiguationData":[OSD([subQ59,subQ65,subQ71,subQ80,subQ54,subQ50,subQ43,subQ79,subQ36,subQ32,subQ27,subQ82,subQ58,subQ84,subQ86,subQ88])],"isStart":false})})})});}
            var sketch = newSketch(context, id + "F10", { "sketchPlane" : qUnion([Q0])});
            skCircle(sketch, "E130", {"center": v(30.27, 12.73) * mm, "radius": 4.23 * mm});
            skPoint(sketch, "E130.centerSnap0", {"position": v(30.27, 53.09) * mm});
            skCircle(sketch, "E131", {"center": v(87.86, 12.73) * mm, "radius": 4.23 * mm});
            skCircle(sketch, "E132", {"center": v(144.45, 12.73) * mm, "radius": 4.2 * mm});
            skSolve(sketch);
        }
        {
            var Q0;
            Q0=makeQuery(id+"F10.imprint","IMPRINT",FACE,{"disambiguationData":[TD([[makeQuery(id+"F10.imprint","IMPRINT",EDGE,{"derivedFrom":sQuery(id+"F10.wireOp",EDGE,"E131")}),1.0]])]});
            var Q1;
            Q1=makeQuery(id+"F10.imprint","IMPRINT",FACE,{"disambiguationData":[TD([[makeQuery(id+"F10.imprint","IMPRINT",EDGE,{"derivedFrom":sQuery(id+"F10.wireOp",EDGE,"E132")}),1.0]])]});
            var Q2;
            Q2=makeQuery(id+"F10.imprint","IMPRINT",FACE,{"disambiguationData":[TD([[makeQuery(id+"F10.imprint","IMPRINT",EDGE,{"derivedFrom":sQuery(id+"F10.wireOp",EDGE,"E130")}),1.0]])]});
            extrude(context, id + "F11", {"entities" : qUnion([Q0, Q1, Q2]), "operationType" : NewBodyOperationType.ADD, "depth" : 25.4 * mm, "offsetDistance" : 25.4 * mm});
        }
        {
            var Q0;
            Q0=makeQuery(id+"F11.opExtrude","CAP_EDGE",EDGE,{"disambiguationData":[OSD([sQuery(id+"F10.wireOp",EDGE,"E130")])],"isStart":false});
            var Q1;
            Q1=makeQuery(id+"F11.opExtrude","CAP_EDGE",EDGE,{"disambiguationData":[OSD([sQuery(id+"F10.wireOp",EDGE,"E131")])],"isStart":false});
            var Q2;
            Q2=makeQuery(id+"F11.opExtrude","CAP_EDGE",EDGE,{"disambiguationData":[OSD([sQuery(id+"F10.wireOp",EDGE,"E132")])],"isStart":false});
            fillet(context, id + "F12", {"entities" : qUnion([Q0, Q1, Q2]), "radius" : 2.03 * mm, "tangentPropagation" : true, "allowEdgeOverflow" : false});
        }
        {
            var Q0;
            {var subQ0=sQuery(id+"F0.wireOp",EDGE,"E12.MirrorCS");var subQ1=sQuery(id+"F0.wireOp",EDGE,"E10.MirrorCS");var subQ2=sQuery(id+"F0.wireOp",EDGE,"E9.MirrorCS");var subQ3=sQuery(id+"F0.wireOp",EDGE,"E7.filletArc");var subQ4=sQuery(id+"F0.wireOp",EDGE,"E6");var subQ5=sQuery(id+"F0.wireOp",EDGE,"E5");var subQ6=sQuery(id+"F0.wireOp",EDGE,"E14.MirrorCS");var subQ7=sQuery(id+"F0.wireOp",EDGE,"E0");var subQ8=sQuery(id+"F0.wireOp",EDGE,"E1");var subQ9=sQuery(id+"F0.wireOp",EDGE,"E2");var subQ10=sQuery(id+"F0.wireOp",EDGE,"E8.MirrorCS");var subQ11=sQuery(id+"F0.wireOp",EDGE,"E3");var subQ12=sQuery(id+"F0.wireOp",EDGE,"E13.MirrorCS");var subQ13=sQuery(id+"F0.wireOp",EDGE,"E15.MirrorCS");var subQ14=sQuery(id+"F0.wireOp",EDGE,"E16.filletArc");var subQ15=sQuery(id+"F0.wireOp",EDGE,"E17.filletArc");Q0=makeQuery(id+"F6.boolean.opBoolean","SPLIT",FACE,{"disambiguationData":[TD([makeQuery(id+"F6.opExtrude","SWEPT_FACE",FACE,{"disambiguationData":[OSD([sQuery(id+"F5.wireOp",EDGE,"E66")])]})])],"derivedFrom":makeQuery(id+"F3.boolean.opBoolean","SPLIT",FACE,{"disambiguationData":[TD([makeQuery(id+"F1.opExtrude","SWEPT_FACE",FACE,{"disambiguationData":[OSD([subQ8])]})])],"derivedFrom":makeQuery(id+"F1.opExtrude","CAP_FACE",FACE,{"disambiguationData":[OSD([subQ7,subQ8,subQ9,subQ11,subQ5,subQ4,subQ3,subQ10,subQ2,subQ1,subQ0,subQ12,subQ6,subQ13,subQ14,subQ15])],"isStart":false})})});}
            var Q1;
            {var subQ0=sQuery(id+"F0.wireOp",EDGE,"E12.MirrorCS");var subQ1=sQuery(id+"F0.wireOp",EDGE,"E10.MirrorCS");var subQ2=sQuery(id+"F0.wireOp",EDGE,"E9.MirrorCS");var subQ3=sQuery(id+"F0.wireOp",EDGE,"E7.filletArc");var subQ4=sQuery(id+"F0.wireOp",EDGE,"E6");var subQ5=sQuery(id+"F0.wireOp",EDGE,"E5");var subQ6=sQuery(id+"F0.wireOp",EDGE,"E14.MirrorCS");var subQ7=sQuery(id+"F0.wireOp",EDGE,"E0");var subQ8=sQuery(id+"F0.wireOp",EDGE,"E1");var subQ9=sQuery(id+"F0.wireOp",EDGE,"E2");var subQ10=sQuery(id+"F0.wireOp",EDGE,"E8.MirrorCS");var subQ11=sQuery(id+"F0.wireOp",EDGE,"E3");var subQ12=sQuery(id+"F0.wireOp",EDGE,"E13.MirrorCS");var subQ13=sQuery(id+"F0.wireOp",EDGE,"E15.MirrorCS");var subQ14=sQuery(id+"F0.wireOp",EDGE,"E16.filletArc");var subQ15=sQuery(id+"F0.wireOp",EDGE,"E17.filletArc");Q1=makeQuery(id+"F6.boolean.opBoolean","SPLIT",FACE,{"disambiguationData":[TD([makeQuery(id+"F6.opExtrude","SWEPT_FACE",FACE,{"disambiguationData":[OSD([sQuery(id+"F5.wireOp",EDGE,"E76")])]})])],"derivedFrom":makeQuery(id+"F3.boolean.opBoolean","SPLIT",FACE,{"disambiguationData":[TD([makeQuery(id+"F1.opExtrude","SWEPT_FACE",FACE,{"disambiguationData":[OSD([subQ8])]})])],"derivedFrom":makeQuery(id+"F1.opExtrude","CAP_FACE",FACE,{"disambiguationData":[OSD([subQ7,subQ8,subQ9,subQ11,subQ5,subQ4,subQ3,subQ10,subQ2,subQ1,subQ0,subQ12,subQ6,subQ13,subQ14,subQ15])],"isStart":false})})});}
            var Q2;
            {var subQ0=sQuery(id+"F0.wireOp",EDGE,"E12.MirrorCS");var subQ1=sQuery(id+"F0.wireOp",EDGE,"E10.MirrorCS");var subQ2=sQuery(id+"F0.wireOp",EDGE,"E9.MirrorCS");var subQ3=sQuery(id+"F0.wireOp",EDGE,"E7.filletArc");var subQ4=sQuery(id+"F0.wireOp",EDGE,"E6");var subQ5=sQuery(id+"F0.wireOp",EDGE,"E5");var subQ6=sQuery(id+"F0.wireOp",EDGE,"E14.MirrorCS");var subQ7=sQuery(id+"F0.wireOp",EDGE,"E0");var subQ8=sQuery(id+"F0.wireOp",EDGE,"E1");var subQ9=sQuery(id+"F0.wireOp",EDGE,"E2");var subQ10=sQuery(id+"F0.wireOp",EDGE,"E8.MirrorCS");var subQ11=sQuery(id+"F0.wireOp",EDGE,"E3");var subQ12=sQuery(id+"F0.wireOp",EDGE,"E13.MirrorCS");var subQ13=sQuery(id+"F0.wireOp",EDGE,"E15.MirrorCS");var subQ14=sQuery(id+"F0.wireOp",EDGE,"E16.filletArc");var subQ15=sQuery(id+"F0.wireOp",EDGE,"E17.filletArc");Q2=makeQuery(id+"F6.boolean.opBoolean","SPLIT",FACE,{"disambiguationData":[TD([makeQuery(id+"F6.opExtrude","SWEPT_FACE",FACE,{"disambiguationData":[OSD([sQuery(id+"F5.wireOp",EDGE,"E101")])]})])],"derivedFrom":makeQuery(id+"F3.boolean.opBoolean","SPLIT",FACE,{"disambiguationData":[TD([makeQuery(id+"F1.opExtrude","SWEPT_FACE",FACE,{"disambiguationData":[OSD([subQ8])]})])],"derivedFrom":makeQuery(id+"F1.opExtrude","CAP_FACE",FACE,{"disambiguationData":[OSD([subQ7,subQ8,subQ9,subQ11,subQ5,subQ4,subQ3,subQ10,subQ2,subQ1,subQ0,subQ12,subQ6,subQ13,subQ14,subQ15])],"isStart":false})})});}
            var Q3;
            {var subQ0=sQuery(id+"F0.wireOp",EDGE,"E12.MirrorCS");var subQ1=sQuery(id+"F0.wireOp",EDGE,"E10.MirrorCS");var subQ2=sQuery(id+"F0.wireOp",EDGE,"E9.MirrorCS");var subQ3=sQuery(id+"F0.wireOp",EDGE,"E7.filletArc");var subQ4=sQuery(id+"F0.wireOp",EDGE,"E6");var subQ5=sQuery(id+"F0.wireOp",EDGE,"E5");var subQ6=sQuery(id+"F0.wireOp",EDGE,"E14.MirrorCS");var subQ7=sQuery(id+"F0.wireOp",EDGE,"E0");var subQ8=sQuery(id+"F0.wireOp",EDGE,"E1");var subQ9=sQuery(id+"F0.wireOp",EDGE,"E2");var subQ10=sQuery(id+"F0.wireOp",EDGE,"E8.MirrorCS");var subQ11=sQuery(id+"F0.wireOp",EDGE,"E3");var subQ12=sQuery(id+"F0.wireOp",EDGE,"E13.MirrorCS");var subQ13=sQuery(id+"F0.wireOp",EDGE,"E15.MirrorCS");var subQ14=sQuery(id+"F0.wireOp",EDGE,"E16.filletArc");var subQ15=sQuery(id+"F0.wireOp",EDGE,"E17.filletArc");Q3=makeQuery(id+"F6.boolean.opBoolean","SPLIT",FACE,{"disambiguationData":[TD([makeQuery(id+"F6.opExtrude","SWEPT_FACE",FACE,{"disambiguationData":[OSD([sQuery(id+"F5.wireOp",EDGE,"E113")])]})])],"derivedFrom":makeQuery(id+"F3.boolean.opBoolean","SPLIT",FACE,{"disambiguationData":[TD([makeQuery(id+"F1.opExtrude","SWEPT_FACE",FACE,{"disambiguationData":[OSD([subQ8])]})])],"derivedFrom":makeQuery(id+"F1.opExtrude","CAP_FACE",FACE,{"disambiguationData":[OSD([subQ7,subQ8,subQ9,subQ11,subQ5,subQ4,subQ3,subQ10,subQ2,subQ1,subQ0,subQ12,subQ6,subQ13,subQ14,subQ15])],"isStart":false})})});}
            var Q4;
            {var subQ0=sQuery(id+"F0.wireOp",EDGE,"E12.MirrorCS");var subQ1=sQuery(id+"F0.wireOp",EDGE,"E10.MirrorCS");var subQ2=sQuery(id+"F0.wireOp",EDGE,"E9.MirrorCS");var subQ3=sQuery(id+"F0.wireOp",EDGE,"E7.filletArc");var subQ4=sQuery(id+"F0.wireOp",EDGE,"E6");var subQ5=sQuery(id+"F0.wireOp",EDGE,"E5");var subQ6=sQuery(id+"F0.wireOp",EDGE,"E14.MirrorCS");var subQ7=sQuery(id+"F0.wireOp",EDGE,"E0");var subQ8=sQuery(id+"F0.wireOp",EDGE,"E1");var subQ9=sQuery(id+"F0.wireOp",EDGE,"E2");var subQ10=sQuery(id+"F0.wireOp",EDGE,"E8.MirrorCS");var subQ11=sQuery(id+"F0.wireOp",EDGE,"E3");var subQ12=sQuery(id+"F0.wireOp",EDGE,"E13.MirrorCS");var subQ13=sQuery(id+"F0.wireOp",EDGE,"E15.MirrorCS");var subQ14=sQuery(id+"F0.wireOp",EDGE,"E16.filletArc");var subQ15=sQuery(id+"F0.wireOp",EDGE,"E17.filletArc");Q4=makeQuery(id+"F6.boolean.opBoolean","SPLIT",FACE,{"disambiguationData":[TD([makeQuery(id+"F6.opExtrude","SWEPT_FACE",FACE,{"disambiguationData":[OSD([sQuery(id+"F5.wireOp",EDGE,"E80")])]})])],"derivedFrom":makeQuery(id+"F3.boolean.opBoolean","SPLIT",FACE,{"disambiguationData":[TD([makeQuery(id+"F1.opExtrude","SWEPT_FACE",FACE,{"disambiguationData":[OSD([subQ8])]})])],"derivedFrom":makeQuery(id+"F1.opExtrude","CAP_FACE",FACE,{"disambiguationData":[OSD([subQ7,subQ8,subQ9,subQ11,subQ5,subQ4,subQ3,subQ10,subQ2,subQ1,subQ0,subQ12,subQ6,subQ13,subQ14,subQ15])],"isStart":false})})});}
            var Q5;
            {var subQ0=sQuery(id+"F0.wireOp",EDGE,"E12.MirrorCS");var subQ1=sQuery(id+"F0.wireOp",EDGE,"E10.MirrorCS");var subQ2=sQuery(id+"F0.wireOp",EDGE,"E9.MirrorCS");var subQ3=sQuery(id+"F0.wireOp",EDGE,"E7.filletArc");var subQ4=sQuery(id+"F0.wireOp",EDGE,"E6");var subQ5=sQuery(id+"F0.wireOp",EDGE,"E5");var subQ6=sQuery(id+"F0.wireOp",EDGE,"E14.MirrorCS");var subQ7=sQuery(id+"F0.wireOp",EDGE,"E0");var subQ8=sQuery(id+"F0.wireOp",EDGE,"E1");var subQ9=sQuery(id+"F0.wireOp",EDGE,"E2");var subQ10=sQuery(id+"F0.wireOp",EDGE,"E8.MirrorCS");var subQ11=sQuery(id+"F0.wireOp",EDGE,"E3");var subQ12=sQuery(id+"F0.wireOp",EDGE,"E13.MirrorCS");var subQ13=sQuery(id+"F0.wireOp",EDGE,"E15.MirrorCS");var subQ14=sQuery(id+"F0.wireOp",EDGE,"E16.filletArc");var subQ15=sQuery(id+"F0.wireOp",EDGE,"E17.filletArc");Q5=makeQuery(id+"F6.boolean.opBoolean","SPLIT",FACE,{"disambiguationData":[TD([makeQuery(id+"F6.opExtrude","SWEPT_FACE",FACE,{"disambiguationData":[OSD([sQuery(id+"F5.wireOp",EDGE,"E91")])]})])],"derivedFrom":makeQuery(id+"F3.boolean.opBoolean","SPLIT",FACE,{"disambiguationData":[TD([makeQuery(id+"F1.opExtrude","SWEPT_FACE",FACE,{"disambiguationData":[OSD([subQ8])]})])],"derivedFrom":makeQuery(id+"F1.opExtrude","CAP_FACE",FACE,{"disambiguationData":[OSD([subQ7,subQ8,subQ9,subQ11,subQ5,subQ4,subQ3,subQ10,subQ2,subQ1,subQ0,subQ12,subQ6,subQ13,subQ14,subQ15])],"isStart":false})})});}
            chamfer(context, id + "F13", {"entities" : qUnion([Q0, Q1, Q2, Q3, Q4, Q5]), "width" : 0.25 * mm, "tangentPropagation" : true});
        }
        {
            var Q0;
            Q0=makeQuery(id+"F6.boolean.opBoolean","COPY",EDGE,{"derivedFrom":makeQuery(id+"F6.opExtrude","CAP_EDGE",EDGE,{"disambiguationData":[OSD([sQuery(id+"F5.wireOp",EDGE,"E62")])],"isStart":true})});
            var Q1;
            Q1=makeQuery(id+"F6.boolean.opBoolean","COPY",EDGE,{"derivedFrom":makeQuery(id+"F6.opExtrude","CAP_EDGE",EDGE,{"disambiguationData":[OSD([sQuery(id+"F5.wireOp",EDGE,"E65")])],"isStart":true})});
            fillet(context, id + "F14", {"entities" : qUnion([Q0, Q1]), "radius" : 1.52 * mm, "tangentPropagation" : true, "allowEdgeOverflow" : false});
        }
        {
            var Q0;
            Q0=makeQuery(id+"F6.boolean.opBoolean","COPY",EDGE,{"derivedFrom":makeQuery(id+"F6.opExtrude","CAP_EDGE",EDGE,{"disambiguationData":[OSD([sQuery(id+"F5.wireOp",EDGE,"E63")])],"isStart":true})});
            var Q1;
            Q1=makeQuery(id+"F6.boolean.opBoolean","COPY",EDGE,{"derivedFrom":makeQuery(id+"F6.opExtrude","CAP_EDGE",EDGE,{"disambiguationData":[OSD([sQuery(id+"F5.wireOp",EDGE,"E64")])],"isStart":true})});
            var Q2;
            Q2=makeQuery(id+"F6.boolean.opBoolean","COPY",EDGE,{"derivedFrom":makeQuery(id+"F6.opExtrude","CAP_EDGE",EDGE,{"disambiguationData":[OSD([sQuery(id+"F5.wireOp",EDGE,"E125.left")])],"isStart":true})});
            var Q3;
            Q3=makeQuery(id+"F6.boolean.opBoolean","COPY",EDGE,{"derivedFrom":makeQuery(id+"F6.opExtrude","CAP_EDGE",EDGE,{"disambiguationData":[OSD([sQuery(id+"F5.wireOp",EDGE,"E127")])],"isStart":true})});
            var Q4;
            Q4=makeQuery(id+"F6.boolean.opBoolean","COPY",EDGE,{"derivedFrom":makeQuery(id+"F6.opExtrude","CAP_EDGE",EDGE,{"disambiguationData":[OSD([sQuery(id+"F5.wireOp",EDGE,"E125.bottom")])],"isStart":true})});
            var Q5;
            Q5=makeQuery(id+"F6.boolean.opBoolean","COPY",EDGE,{"derivedFrom":makeQuery(id+"F6.opExtrude","CAP_EDGE",EDGE,{"disambiguationData":[OSD([sQuery(id+"F5.wireOp",EDGE,"E126")])],"isStart":true})});
            var Q6;
            Q6=makeQuery(id+"F6.boolean.opBoolean","COPY",EDGE,{"derivedFrom":makeQuery(id+"F6.opExtrude","CAP_EDGE",EDGE,{"disambiguationData":[OSD([sQuery(id+"F5.wireOp",EDGE,"E125.right")])],"isStart":true})});
            var Q7;
            Q7=makeQuery(id+"F6.boolean.opBoolean","COPY",EDGE,{"derivedFrom":makeQuery(id+"F6.opExtrude","CAP_EDGE",EDGE,{"disambiguationData":[OSD([sQuery(id+"F5.wireOp",EDGE,"E125.top")])],"isStart":true})});
            var Q8;
            Q8=makeQuery(id+"F6.boolean.opBoolean","COPY",EDGE,{"derivedFrom":makeQuery(id+"F6.opExtrude","CAP_EDGE",EDGE,{"disambiguationData":[OSD([sQuery(id+"F5.wireOp",EDGE,"E129")])],"isStart":true})});
            chamfer(context, id + "F15", {"entities" : qUnion([Q0, Q1, Q2, Q3, Q4, Q5, Q6, Q7, Q8]), "width" : 0.25 * mm, "tangentPropagation" : true});
        }
        {
            var Q0;
            Q0=qCreatedBy(makeId("Right.planeOp"),FACE);
            var sketch = newSketch(context, id + "F16", { "sketchPlane" : qUnion([Q0])});
            skArc(sketch, "E133", {"start": v(17.01, 24.43) * mm, "mid": v(15.75, 21.64) * mm, "end": v(17.03, 18.85) * mm});
            skLineSegment(sketch, "E134", {"start": v(17.01, 24.43) * mm, "end": v(17.03, 18.85) * mm});
            skSolve(sketch);
        }
        {
            var Q0;
            Q0 = qSketchRegion(id + "F16", true);
            extrude(context, id + "F17", {"entities" : qUnion([Q0]), "operationType" : NewBodyOperationType.REMOVE, "endBound" : BoundingType.THROUGH_ALL, "depth" : 25.4 * mm, "offsetDistance" : 25.4 * mm});
        }
    });
